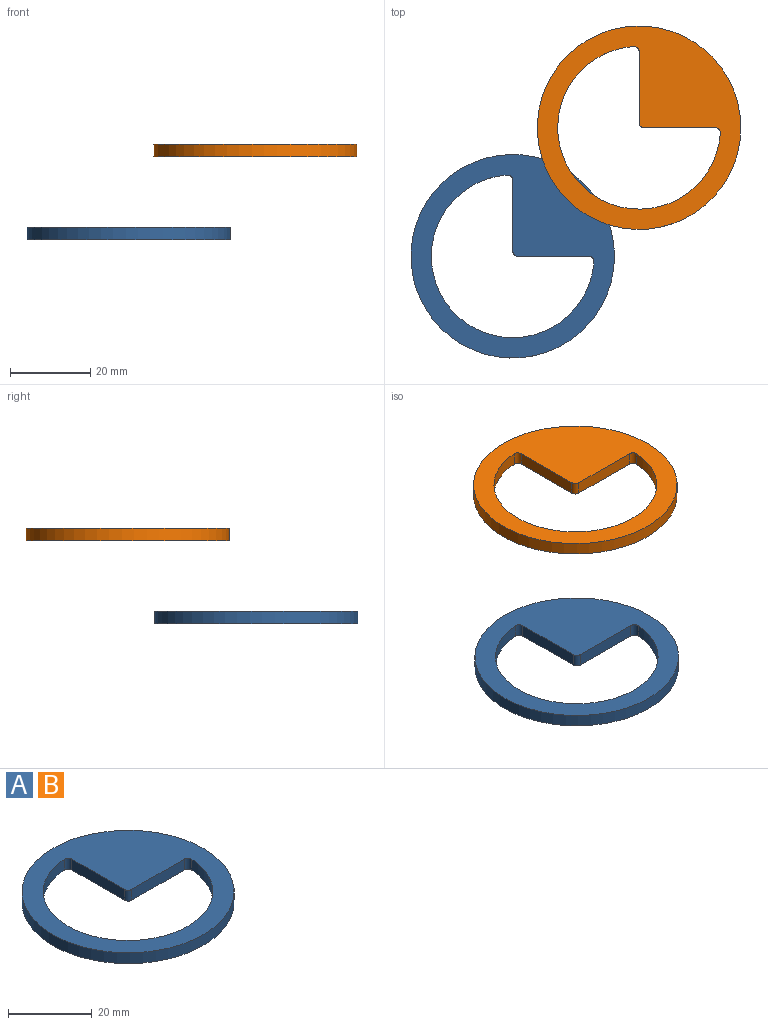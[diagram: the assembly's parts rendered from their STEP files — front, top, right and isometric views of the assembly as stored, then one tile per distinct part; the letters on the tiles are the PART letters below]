
ASSEMBLY  parts=2 mates=1
PART A: 9 faces, bbox 50.8x50.8x3.2 mm
  f0: cylinder r=20.32mm len=40.59mm, axis (0,0,-1), area 295.4mm2, adj f4,f5,f6,f7
  f1: plane 17.74x3.18mm, normal (-1,0,0), area 56.3mm2, adj f4,f5,f7,f8
  f2: plane 17.74x3.18mm, normal (0,-1,0), area 56.3mm2, adj f4,f5,f6,f8
  f3: cylinder r=25.4mm len=50.8mm, axis (0,0,-1), area 506.7mm2, adj f4,f5
  f4: plane 50.8x50.8mm, normal (0,0,1), area 1054.4mm2, adj f0,f1,f2,f3,f6,f7,f8
  f5: plane 50.8x50.8mm, normal (0,0,-1), area 1054.4mm2, adj f0,f1,f2,f3,f6,f7,f8
  f6: cylinder r=1.27mm len=3.18mm, axis (0,0,-1), area 6.6mm2, adj f0,f2,f4,f5
  f7: cylinder r=1.27mm len=3.18mm, axis (0,0,-1), area 6.6mm2, adj f0,f1,f4,f5
  f8: cylinder r=1.27mm len=3.18mm, axis (0,0,-1), area 6.3mm2, adj f1,f2,f4,f5
PART B: same geometry as A
PLACE A t=(-40.2,-35.49,-20)mm
PLACE B t=(-8.66,-3.45,0.74)mm
MATE parallel B.f4 <-> A.f4  axis (0,0,1) through (-6,-0.79,3.92)mm
